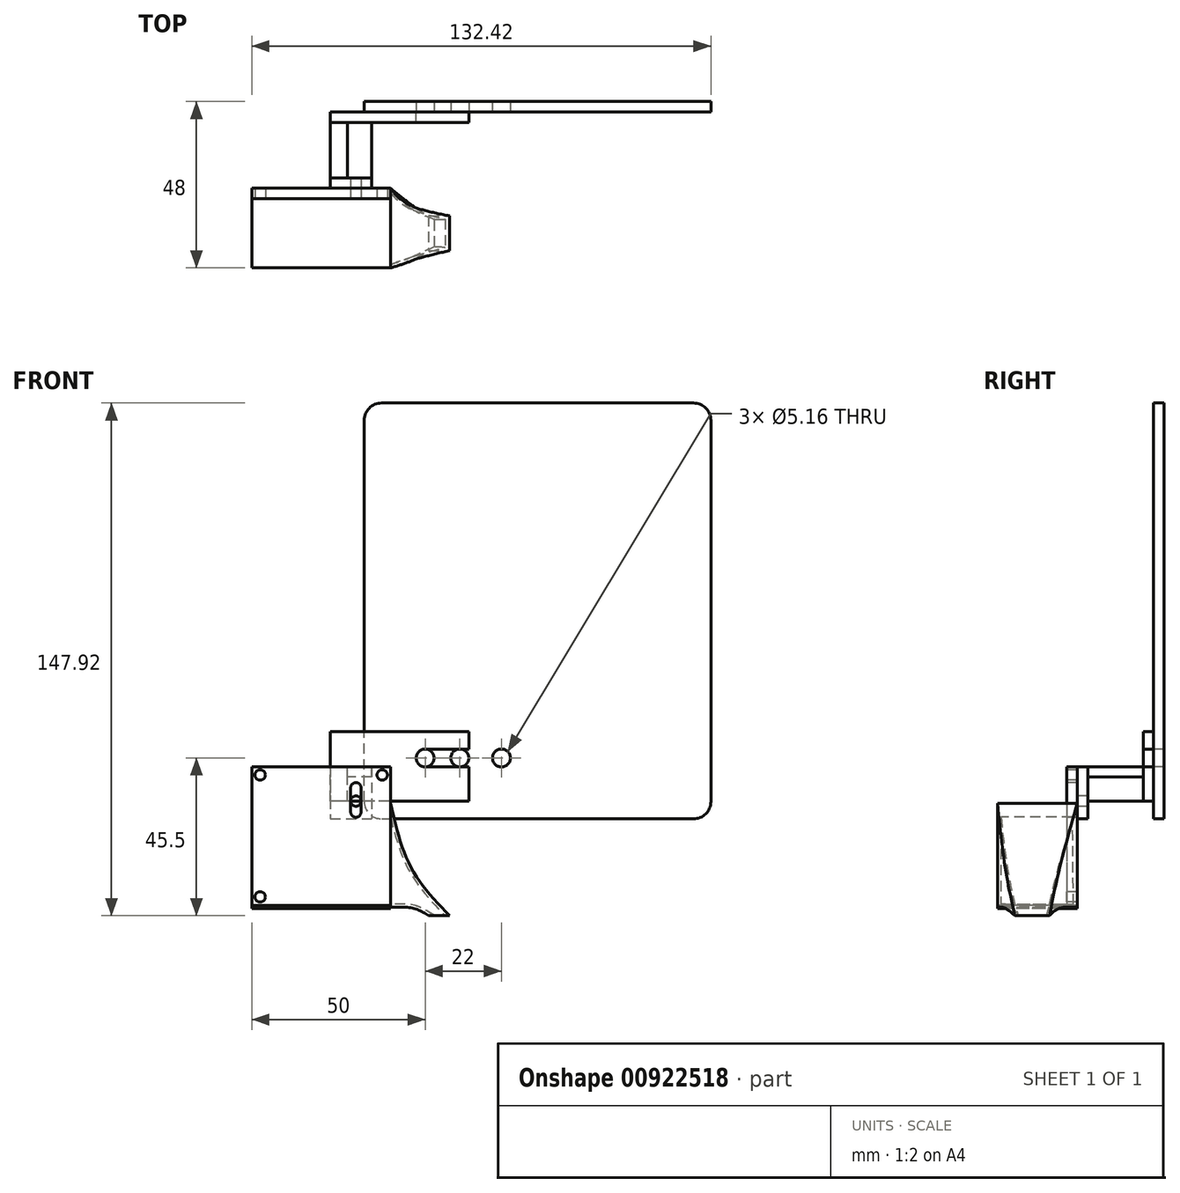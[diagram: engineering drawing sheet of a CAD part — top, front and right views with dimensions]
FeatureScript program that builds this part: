
annotation { "Feature Type Name" : "Feature", "Feature Type Description" : "" }
export const myFeature = defineFeature(function(context is Context, id is Id, definition is map)
    precondition{}
    {
        {
            var Q0;
            Q0=qCreatedBy(makeId("Front.planeOp"),FACE);
            var sketch = newSketch(context, id + "F0", { "sketchPlane" : qUnion([Q0])});
            skLineSegment(sketch, "E0", {"start": v(-70.29, 0) * mm, "end": v(66.15, 0) * mm, "construction": true});
            skSolve(sketch);
        }
        {
            var Q0;
            Q0=qCreatedBy(makeId("Front.planeOp"),FACE);
            var sketch = newSketch(context, id + "F1", { "sketchPlane" : qUnion([Q0])});
            skLineSegment(sketch, "E1", {"start": v(-102.75, 45.5) * mm, "end": v(100.03, 45.5) * mm, "construction": true});
            skSolve(sketch);
        }
        {
            var Q0;
            Q0=qCreatedBy(makeId("Front.planeOp"),FACE);
            var sketch = newSketch(context, id + "F2", { "sketchPlane" : qUnion([Q0])});
            skLineSegment(sketch, "E2", {"start": v(0, 59.23) * mm, "end": v(0, -34.81) * mm, "construction": true});
            skSolve(sketch);
        }
        {
            var Q0;
            Q0=qCreatedBy(makeId("Front.planeOp"),FACE);
            var sketch = newSketch(context, id + "F3", { "sketchPlane" : qUnion([Q0])});
            skCircle(sketch, "E3", {"center": v(0, 45.5) * mm, "radius": 2.58 * mm});
            skCircle(sketch, "E4", {"center": v(-10, 45.5) * mm, "radius": 2.58 * mm});
            skCircle(sketch, "E5", {"center": v(12, 45.5) * mm, "radius": 2.58 * mm});
            skLineSegment(sketch, "E6.bottom", {"start": v(-22.58, 27.92) * mm, "end": v(67.42, 27.92) * mm});
            skLineSegment(sketch, "E6.top", {"start": v(-22.58, 147.92) * mm, "end": v(67.42, 147.92) * mm});
            skLineSegment(sketch, "E6.left", {"start": v(-27.58, 32.92) * mm, "end": v(-27.58, 142.92) * mm});
            skLineSegment(sketch, "E6.right", {"start": v(72.42, 32.92) * mm, "end": v(72.42, 142.92) * mm});
            skPoint(sketch, "E7.visualSharp", {"position": v(-27.58, 27.92) * mm});
            skArc(sketch, "E7.filletArc", {"start": v(-27.58, 32.92) * mm, "mid": v(-26.12, 29.38) * mm, "end": v(-22.58, 27.92) * mm});
            skPoint(sketch, "E8.visualSharp", {"position": v(72.42, 27.92) * mm});
            skArc(sketch, "E8.filletArc", {"start": v(67.42, 27.92) * mm, "mid": v(70.96, 29.38) * mm, "end": v(72.42, 32.92) * mm});
            skPoint(sketch, "E9.visualSharp", {"position": v(-27.58, 147.92) * mm});
            skArc(sketch, "E9.filletArc", {"start": v(-22.58, 147.92) * mm, "mid": v(-26.12, 146.46) * mm, "end": v(-27.58, 142.92) * mm});
            skPoint(sketch, "E10.visualSharp", {"position": v(72.42, 147.92) * mm});
            skArc(sketch, "E10.filletArc", {"start": v(72.42, 142.92) * mm, "mid": v(70.96, 146.46) * mm, "end": v(67.42, 147.92) * mm});
            skSolve(sketch);
        }
        {
            var Q0;
            Q0=makeQuery(id+"F3.imprint","IMPRINT",FACE,{"disambiguationData":[TD([[makeQuery(id+"F3.imprint","IMPRINT",EDGE,{"derivedFrom":sQuery(id+"F3.wireOp",EDGE,"E3")}),-1.0]])]});
            extrude(context, id + "F4", {"entities" : qUnion([Q0]), "oppositeDirection" : true, "depth" : 3 * mm, "offsetDistance" : 25 * mm});
        }
        {
            var Q0;
            Q0=makeQuery(id+"F4.opExtrude","CAP_EDGE",EDGE,{"disambiguationData":[OSD([sQuery(id+"F3.wireOp",EDGE,"E6.bottom")])],"isStart":false});
            cPoint(context, id + "F5", {"entities" : qUnion([Q0]), "parameter" : 0.5});
        }
        {
            var Q0;
            Q0=makeQuery(id+"F4.opExtrude","CAP_VERTEX",VERTEX,{"disambiguationData":[OSD([sQuery(id+"F3.wireOp",EDGE,"E6.bottom"),sQuery(id+"F3.wireOp",EDGE,"E8.filletArc")])],"isStart":true});
            var Q1;
            Q1=makeQuery(id+"F4.opExtrude","CAP_VERTEX",VERTEX,{"disambiguationData":[OSD([sQuery(id+"F3.wireOp",EDGE,"E6.bottom"),sQuery(id+"F3.wireOp",EDGE,"E7.filletArc")])],"isStart":true});
            var Q2;
            Q2 = qCreatedBy(id + "F5" ,VERTEX);
            cPlane(context, id + "F6", {"entities" : qUnion([Q0, Q1, Q2]), "cplaneType" : CPlaneType.THREE_POINT, "offset" : 25 * mm, "width" : 150 * mm, "height" : 150 * mm});
        }
        {
            var Q0;
            Q0=qCreatedBy(makeId("Front.planeOp"),FACE);
            cPlane(context, id + "F7", {"entities" : qUnion([Q0]), "cplaneType" : CPlaneType.OFFSET, "offset" : 35 * mm, "width" : 150 * mm, "height" : 150 * mm});
        }
        {
            var Q0;
            Q0=qCreatedBy(id+"F7.planeOp",FACE);
            var sketch = newSketch(context, id + "F8", { "sketchPlane" : qUnion([Q0])});
            skLineSegment(sketch, "E11", {"start": v(0, -44.4) * mm, "end": v(0, 80.85) * mm, "construction": true});
            skLineSegment(sketch, "E12", {"start": v(-69.9, 0) * mm, "end": v(66.63, 0) * mm, "construction": true});
            skSolve(sketch);
        }
        {
            var Q0;
            Q0=sQuery(id+"F8.wireOp",EDGE,"E12");
            cPoint(context, id + "F9", {"entities" : qUnion([Q0]), "parameter" : 0.5});
        }
        {
            var Q0;
            Q0=makeQuery(id+"F3.imprint","IMPRINT",FACE,{"disambiguationData":[TD([[makeQuery(id+"F3.imprint","IMPRINT",EDGE,{"derivedFrom":sQuery(id+"F3.wireOp",EDGE,"E3")}),-1.0]])]});
            var Q1;
            Q1 = qCreatedBy(id + "F9" ,VERTEX);
            cPlane(context, id + "F10", {"entities" : qUnion([Q0, Q1]), "cplaneType" : CPlaneType.PLANE_POINT, "offset" : 25 * mm, "width" : 150 * mm, "height" : 150 * mm});
        }
        {
            var Q0;
            Q0=qCreatedBy(id+"F10.planeOp",FACE);
            cPlane(context, id + "F11", {"entities" : qUnion([Q0]), "cplaneType" : CPlaneType.OFFSET, "offset" : 10 * mm, "oppositeDirection" : true, "width" : 150 * mm, "height" : 150 * mm});
        }
        {
            var Q0;
            Q0=qCreatedBy(id+"F11.planeOp",FACE);
            var sketch = newSketch(context, id + "F12", { "sketchPlane" : qUnion([Q0])});
            skLineSegment(sketch, "E13.bottom", {"start": v(-60, 43) * mm, "end": v(-20, 43) * mm});
            skLineSegment(sketch, "E13.top", {"start": v(-60, 3) * mm, "end": v(-20, 3) * mm});
            skLineSegment(sketch, "E13.left", {"start": v(-60, 43) * mm, "end": v(-60, 3) * mm});
            skLineSegment(sketch, "E13.right", {"start": v(-20, 43) * mm, "end": v(-20, 3) * mm});
            skCircle(sketch, "E14", {"center": v(-57.6, 40.6) * mm, "radius": 1.5 * mm});
            skCircle(sketch, "E15", {"center": v(-22.4, 40.6) * mm, "radius": 1.5 * mm});
            skCircle(sketch, "E16", {"center": v(-57.6, 5.4) * mm, "radius": 1.5 * mm});
            skLineSegment(sketch, "E17.bottom", {"start": v(-29.98, 38.38) * mm, "end": v(-29.98, 38.38) * mm});
            skLineSegment(sketch, "E17.top", {"start": v(-29.98, 28.38) * mm, "end": v(-29.98, 28.38) * mm});
            skLineSegment(sketch, "E17.left", {"start": v(-31.48, 36.88) * mm, "end": v(-31.48, 29.88) * mm});
            skLineSegment(sketch, "E17.right", {"start": v(-28.48, 36.88) * mm, "end": v(-28.48, 29.88) * mm});
            skPoint(sketch, "E18.visualSharp", {"position": v(-31.48, 38.38) * mm});
            skArc(sketch, "E18.filletArc", {"start": v(-29.98, 38.38) * mm, "mid": v(-31.04, 37.95) * mm, "end": v(-31.48, 36.88) * mm});
            skPoint(sketch, "E19.visualSharp", {"position": v(-28.48, 38.38) * mm});
            skArc(sketch, "E19.filletArc", {"start": v(-28.48, 36.88) * mm, "mid": v(-28.92, 37.95) * mm, "end": v(-29.98, 38.38) * mm});
            skPoint(sketch, "E20.visualSharp", {"position": v(-31.48, 28.38) * mm});
            skArc(sketch, "E20.filletArc", {"start": v(-31.48, 29.88) * mm, "mid": v(-31.04, 28.82) * mm, "end": v(-29.98, 28.38) * mm});
            skPoint(sketch, "E21.visualSharp", {"position": v(-28.48, 28.38) * mm});
            skArc(sketch, "E21.filletArc", {"start": v(-29.98, 28.38) * mm, "mid": v(-28.92, 28.82) * mm, "end": v(-28.48, 29.88) * mm});
            skSolve(sketch);
        }
        {
            var Q0;
            Q0=makeQuery(id+"F12.imprint","IMPRINT",FACE,{"disambiguationData":[TD([[makeQuery(id+"F12.imprint","IMPRINT",EDGE,{"derivedFrom":sQuery(id+"F12.wireOp",EDGE,"E13.bottom")}),-1.0]])]});
            extrude(context, id + "F13", {"entities" : qUnion([Q0]), "oppositeDirection" : true, "depth" : 3 * mm, "offsetDistance" : 25 * mm});
        }
        {
            var Q0;
            Q0=makeQuery(id+"F13.opExtrude","CAP_EDGE",EDGE,{"disambiguationData":[OSD([sQuery(id+"F12.wireOp",EDGE,"E13.right")])],"isStart":true});
            cPoint(context, id + "F14", {"entities" : qUnion([Q0]), "parameter" : 0.5});
        }
        {
            var Q0;
            Q0=makeQuery(id+"F13.opExtrude","SWEPT_FACE",FACE,{"disambiguationData":[OSD([sQuery(id+"F12.wireOp",EDGE,"E13.right")])]});
            var Q1;
            Q1 = qCreatedBy(id + "F14" ,VERTEX);
            cPlane(context, id + "F15", {"entities" : qUnion([Q0, Q1]), "cplaneType" : CPlaneType.PLANE_POINT, "offset" : 25 * mm, "width" : 150 * mm, "height" : 150 * mm});
        }
        {
            var Q0;
            Q0=qCreatedBy(id+"F15.planeOp",FACE);
            var sketch = newSketch(context, id + "F16", { "sketchPlane" : qUnion([Q0])});
            skLineSegment(sketch, "E22.bottom", {"start": v(-22, 2.4) * mm, "end": v(-45, 2.4) * mm});
            skLineSegment(sketch, "E22.top", {"start": v(-22, 32.4) * mm, "end": v(-45, 32.4) * mm});
            skLineSegment(sketch, "E22.left", {"start": v(-22, 2.4) * mm, "end": v(-22, 32.4) * mm});
            skLineSegment(sketch, "E22.right", {"start": v(-45, 2.4) * mm, "end": v(-45, 32.4) * mm});
            skSolve(sketch);
        }
        {
            var Q0;
            Q0=qCreatedBy(makeId("Top.planeOp"),FACE);
            var sketch = newSketch(context, id + "F17", { "sketchPlane" : qUnion([Q0])});
            skLineSegment(sketch, "E23.bottom", {"start": v(-9, -30) * mm, "end": v(-3, -30) * mm});
            skLineSegment(sketch, "E23.top", {"start": v(-9, -40) * mm, "end": v(-3, -40) * mm});
            skLineSegment(sketch, "E23.left", {"start": v(-9, -30) * mm, "end": v(-9, -40) * mm});
            skLineSegment(sketch, "E23.right", {"start": v(-3, -30) * mm, "end": v(-3, -40) * mm});
            skSolve(sketch);
        }
        {
            var Q0;
            Q0=makeQuery(id+"F13.opExtrude","CAP_EDGE",EDGE,{"disambiguationData":[OSD([sQuery(id+"F12.wireOp",EDGE,"E13.top")])],"isStart":false});
            cPoint(context, id + "F18", {"entities" : qUnion([Q0]), "parameter" : 0.5});
        }
        {
            var Q0;
            Q0=makeQuery(id+"F13.opExtrude","SWEPT_FACE",FACE,{"disambiguationData":[OSD([sQuery(id+"F12.wireOp",EDGE,"E13.top")])]});
            var Q1;
            Q1 = qCreatedBy(id + "F18" ,VERTEX);
            cPlane(context, id + "F19", {"entities" : qUnion([Q0, Q1]), "cplaneType" : CPlaneType.PLANE_POINT, "offset" : 25 * mm, "width" : 150 * mm, "height" : 150 * mm});
        }
        {
            var Q0;
            Q0=qCreatedBy(id+"F19.planeOp",FACE);
            var sketch = newSketch(context, id + "F20", { "sketchPlane" : qUnion([Q0])});
            skLineSegment(sketch, "E24.bottom", {"start": v(-60, 22) * mm, "end": v(-19.96, 22) * mm});
            skLineSegment(sketch, "E24.top", {"start": v(-60, 44.99) * mm, "end": v(-19.96, 44.99) * mm});
            skLineSegment(sketch, "E24.left", {"start": v(-60, 22) * mm, "end": v(-60, 44.99) * mm});
            skLineSegment(sketch, "E24.right", {"start": v(-19.96, 22) * mm, "end": v(-19.96, 44.99) * mm});
            skSolve(sketch);
        }
        {
            var Q0;
            Q0=makeQuery(id+"F20.imprint","IMPRINT",FACE,{"disambiguationData":[TD([[makeQuery(id+"F20.imprint","IMPRINT",EDGE,{"derivedFrom":sQuery(id+"F20.wireOp",EDGE,"E24.bottom")}),1.0]])]});
            extrude(context, id + "F21", {"entities" : qUnion([Q0]), "operationType" : NewBodyOperationType.ADD, "depth" : 1 * mm, "offsetDistance" : 25 * mm});
        }
        {
            var Q0;
            Q0=qCreatedBy(makeId("Right.planeOp"),FACE);
            cPlane(context, id + "F22", {"entities" : qUnion([Q0]), "cplaneType" : CPlaneType.OFFSET, "offset" : 13 * mm, "oppositeDirection" : true, "width" : 150 * mm, "height" : 150 * mm});
        }
        {
            var Q0;
            Q0=qCreatedBy(id+"F22.planeOp",FACE);
            var sketch = newSketch(context, id + "F23", { "sketchPlane" : qUnion([Q0])});
            skLineSegment(sketch, "E25.bottom", {"start": v(-42.5, 2) * mm, "end": v(-27.5, 2) * mm});
            skLineSegment(sketch, "E25.top", {"start": v(-42.5, 12) * mm, "end": v(-27.5, 12) * mm});
            skLineSegment(sketch, "E25.left", {"start": v(-42.5, 2) * mm, "end": v(-42.5, 12) * mm});
            skLineSegment(sketch, "E25.right", {"start": v(-27.5, 2) * mm, "end": v(-27.5, 12) * mm});
            skSolve(sketch);
        }
        {
            var Q1;
            Q1=makeQuery(id+"F16.imprint","IMPRINT",FACE,{"disambiguationData":[TD([[makeQuery(id+"F16.imprint","IMPRINT",EDGE,{"derivedFrom":sQuery(id+"F16.wireOp",EDGE,"E22.bottom")}),-1.0]])]});
            var Q2;
            Q2=makeQuery(id+"F23.imprint","IMPRINT",FACE,{"disambiguationData":[TD([[makeQuery(id+"F23.imprint","IMPRINT",EDGE,{"derivedFrom":sQuery(id+"F23.wireOp",EDGE,"E25.bottom")}),1.0]])]});
            var Q3;
            Q3=makeQuery(id+"F17.imprint","IMPRINT",FACE,{"disambiguationData":[TD([[makeQuery(id+"F17.imprint","IMPRINT",EDGE,{"derivedFrom":sQuery(id+"F17.wireOp",EDGE,"E23.bottom")}),-1.0]])]});
            loft(context, id + "F24", {"sheetProfilesArray" : [{ "sheetProfileEntities" : qUnion([Q1]) }, { "sheetProfileEntities" : qUnion([Q2]) }, { "sheetProfileEntities" : qUnion([Q3]) }]});
        }
        {
            var Q0;
            Q0=makeQuery(id+"F24.opLoft","CAP_FACE",FACE,{"disambiguationData":[OSD([makeQuery(id+"F16.imprint","IMPRINT",FACE,{"disambiguationData":[TD([[makeQuery(id+"F16.imprint","IMPRINT",EDGE,{"derivedFrom":sQuery(id+"F16.wireOp",EDGE,"E22.bottom")}),-1.0]])]})])],"isStart":true});
            var Q1;
            Q1=makeQuery(id+"F24.opLoft","CAP_FACE",FACE,{"disambiguationData":[OSD([makeQuery(id+"F17.imprint","IMPRINT",FACE,{"disambiguationData":[TD([[makeQuery(id+"F17.imprint","IMPRINT",EDGE,{"derivedFrom":sQuery(id+"F17.wireOp",EDGE,"E23.bottom")}),-1.0]])]})])],"isStart":true});
            shell(context, id + "F25", {"entities" : qUnion([Q0, Q1]), "thickness" : 0.9 * mm});
        }
        {
            var Q0;
            Q0=qCreatedBy(makeId("Front.planeOp"),FACE);
            var sketch = newSketch(context, id + "F26", { "sketchPlane" : qUnion([Q0])});
            skLineSegment(sketch, "E26.bottom", {"start": v(2.58, 53.08) * mm, "end": v(-37.42, 53.08) * mm});
            skLineSegment(sketch, "E26.top", {"start": v(2.58, 33.08) * mm, "end": v(-37.42, 33.08) * mm});
            skLineSegment(sketch, "E26.left", {"start": v(2.58, 53.08) * mm, "end": v(2.58, 48.08) * mm});
            skLineSegment(sketch, "E26.right", {"start": v(-37.42, 53.08) * mm, "end": v(-37.42, 33.08) * mm});
            skLineSegment(sketch, "E27", {"start": v(-10, 48.08) * mm, "end": v(2.58, 48.08) * mm});
            skLineSegment(sketch, "E28", {"start": v(-10, 42.92) * mm, "end": v(2.58, 42.92) * mm});
            skArc(sketch, "E29", {"start": v(-10, 48.08) * mm, "mid": v(-12.58, 45.5) * mm, "end": v(-10, 42.92) * mm});
            skLineSegment(sketch, "E30.trimOffspring", {"start": v(2.58, 42.92) * mm, "end": v(2.58, 33.08) * mm});
            skSolve(sketch);
        }
        {
            var Q0;
            Q0=makeQuery(id+"F26.imprint","IMPRINT",FACE,{"disambiguationData":[TD([[makeQuery(id+"F26.imprint","IMPRINT",EDGE,{"derivedFrom":sQuery(id+"F26.wireOp",EDGE,"E26.bottom")}),1.0]])]});
            extrude(context, id + "F27", {"entities" : qUnion([Q0]), "depth" : 3 * mm, "offsetDistance" : 25 * mm});
        }
        {
            var Q0;
            Q0=makeQuery(id+"F13.opExtrude","CAP_EDGE",EDGE,{"disambiguationData":[OSD([sQuery(id+"F12.wireOp",EDGE,"E17.left")])],"isStart":false});
            cPoint(context, id + "F28", {"entities" : qUnion([Q0]), "parameter" : 0.5});
        }
        {
            var Q0;
            Q0=makeQuery(id+"F21.boolean.opBoolean","MERGE",FACE,{"derivedFrom":[makeQuery(id+"F13.opExtrude","CAP_FACE",FACE,{"disambiguationData":[OSD([sQuery(id+"F12.wireOp",EDGE,"E13.bottom"),sQuery(id+"F12.wireOp",EDGE,"E13.top"),sQuery(id+"F12.wireOp",EDGE,"E13.left"),sQuery(id+"F12.wireOp",EDGE,"E13.right"),sQuery(id+"F12.wireOp",EDGE,"E14"),sQuery(id+"F12.wireOp",EDGE,"E15"),sQuery(id+"F12.wireOp",EDGE,"E16"),sQuery(id+"F12.wireOp",EDGE,"E17.left"),sQuery(id+"F12.wireOp",EDGE,"E17.right"),sQuery(id+"F12.wireOp",EDGE,"E18.filletArc"),sQuery(id+"F12.wireOp",EDGE,"E19.filletArc"),sQuery(id+"F12.wireOp",EDGE,"E20.filletArc"),sQuery(id+"F12.wireOp",EDGE,"E21.filletArc")])],"isStart":false}),makeQuery(id+"F21.opExtrude","SWEPT_FACE",FACE,{"disambiguationData":[OSD([sQuery(id+"F20.wireOp",EDGE,"E24.bottom")])]})]});
            var Q1;
            Q1 = qCreatedBy(id + "F28" ,VERTEX);
            cPlane(context, id + "F29", {"entities" : qUnion([Q0, Q1]), "cplaneType" : CPlaneType.PLANE_POINT, "offset" : 25 * mm, "width" : 150 * mm, "height" : 150 * mm});
        }
        {
            var Q0;
            Q0=qCreatedBy(id+"F29.planeOp",FACE);
            var sketch = newSketch(context, id + "F30", { "sketchPlane" : qUnion([Q0])});
            skLineSegment(sketch, "E31.bottom", {"start": v(92.62, 98.78) * mm, "end": v(-30.38, 98.78) * mm});
            skLineSegment(sketch, "E31.top", {"start": v(92.62, -29.83) * mm, "end": v(-30.38, -29.83) * mm});
            skLineSegment(sketch, "E31.left", {"start": v(92.62, 98.78) * mm, "end": v(92.62, -29.83) * mm});
            skLineSegment(sketch, "E31.right", {"start": v(-30.38, 98.78) * mm, "end": v(-30.38, -29.83) * mm});
            skLineSegment(sketch, "E32.bottom", {"start": v(37.42, 43) * mm, "end": v(25.42, 43) * mm});
            skLineSegment(sketch, "E32.top", {"start": v(37.42, 28) * mm, "end": v(25.42, 28) * mm});
            skLineSegment(sketch, "E32.left", {"start": v(37.42, 43) * mm, "end": v(37.42, 28) * mm});
            skLineSegment(sketch, "E32.right", {"start": v(25.42, 43) * mm, "end": v(25.42, 28) * mm});
            skCircle(sketch, "E33", {"center": v(29.98, 33.06) * mm, "radius": 1.5 * mm});
            skSolve(sketch);
        }
        {
            var Q0;
            Q0=makeQuery(id+"F30.imprint","IMPRINT",FACE,{"disambiguationData":[TD([[makeQuery(id+"F30.imprint","IMPRINT",EDGE,{"derivedFrom":sQuery(id+"F30.wireOp",EDGE,"E32.bottom")}),1.0]])]});
            extrude(context, id + "F31", {"entities" : qUnion([Q0]), "depth" : 3 * mm, "offsetDistance" : 25 * mm});
        }
        {
            var Q0;
            Q0=makeQuery(id+"F31.opExtrude","CAP_EDGE",EDGE,{"disambiguationData":[OSD([sQuery(id+"F30.wireOp",EDGE,"E32.left")])],"isStart":false});
            cPoint(context, id + "F32", {"entities" : qUnion([Q0]), "parameter" : 0.5});
        }
        {
            var Q0;
            Q0=makeQuery(id+"F31.opExtrude","SWEPT_FACE",FACE,{"disambiguationData":[OSD([sQuery(id+"F30.wireOp",EDGE,"E32.left")])]});
            var Q1;
            Q1 = qCreatedBy(id + "F32" ,VERTEX);
            cPlane(context, id + "F33", {"entities" : qUnion([Q0, Q1]), "cplaneType" : CPlaneType.PLANE_POINT, "offset" : 25 * mm, "width" : 150 * mm, "height" : 150 * mm});
        }
        {
            var Q0;
            Q0=qCreatedBy(id+"F33.planeOp",FACE);
            var sketch = newSketch(context, id + "F34", { "sketchPlane" : qUnion([Q0])});
            skLineSegment(sketch, "E34.bottom", {"start": v(3, 33.08) * mm, "end": v(19, 33.08) * mm});
            skLineSegment(sketch, "E34.top", {"start": v(3, 43) * mm, "end": v(19, 43) * mm});
            skLineSegment(sketch, "E34.left", {"start": v(3, 33.08) * mm, "end": v(3, 43) * mm});
            skLineSegment(sketch, "E34.right", {"start": v(19, 33.08) * mm, "end": v(19, 43) * mm});
            skSolve(sketch);
        }
        {
            var Q0;
            Q0=makeQuery(id+"F34.imprint","IMPRINT",FACE,{"disambiguationData":[TD([[makeQuery(id+"F34.imprint","IMPRINT",EDGE,{"derivedFrom":sQuery(id+"F34.wireOp",EDGE,"E34.bottom")}),1.0]])]});
            extrude(context, id + "F35", {"entities" : qUnion([Q0]), "oppositeDirection" : true, "depth" : 5 * mm, "offsetDistance" : 25 * mm});
        }
        {
            var Q0;
            Q0=makeQuery(id+"F35.opExtrude","CAP_FACE",FACE,{"disambiguationData":[OSD([sQuery(id+"F34.wireOp",EDGE,"E34.bottom"),sQuery(id+"F34.wireOp",EDGE,"E34.top"),sQuery(id+"F34.wireOp",EDGE,"E34.left"),sQuery(id+"F34.wireOp",EDGE,"E34.right")])],"isStart":false});
            var sketch = newSketch(context, id + "F36", { "sketchPlane" : qUnion([Q0])});
            skLineSegment(sketch, "E35.bottom", {"start": v(-19, 43) * mm, "end": v(-3, 43) * mm});
            skLineSegment(sketch, "E35.top", {"start": v(-19, 40) * mm, "end": v(-3, 40) * mm});
            skLineSegment(sketch, "E35.left", {"start": v(-19, 43) * mm, "end": v(-19, 40) * mm});
            skLineSegment(sketch, "E35.right", {"start": v(-3, 43) * mm, "end": v(-3, 40) * mm});
            skSolve(sketch);
        }
        {
            var Q0;
            Q0=makeQuery(id+"F36.imprint","IMPRINT",FACE,{"disambiguationData":[TD([[makeQuery(id+"F36.imprint","IMPRINT",EDGE,{"derivedFrom":sQuery(id+"F36.wireOp",EDGE,"E35.bottom")}),1.0]])]});
            extrude(context, id + "F37", {"entities" : qUnion([Q0]), "depth" : 7 * mm, "offsetDistance" : 25 * mm});
        }
    });
